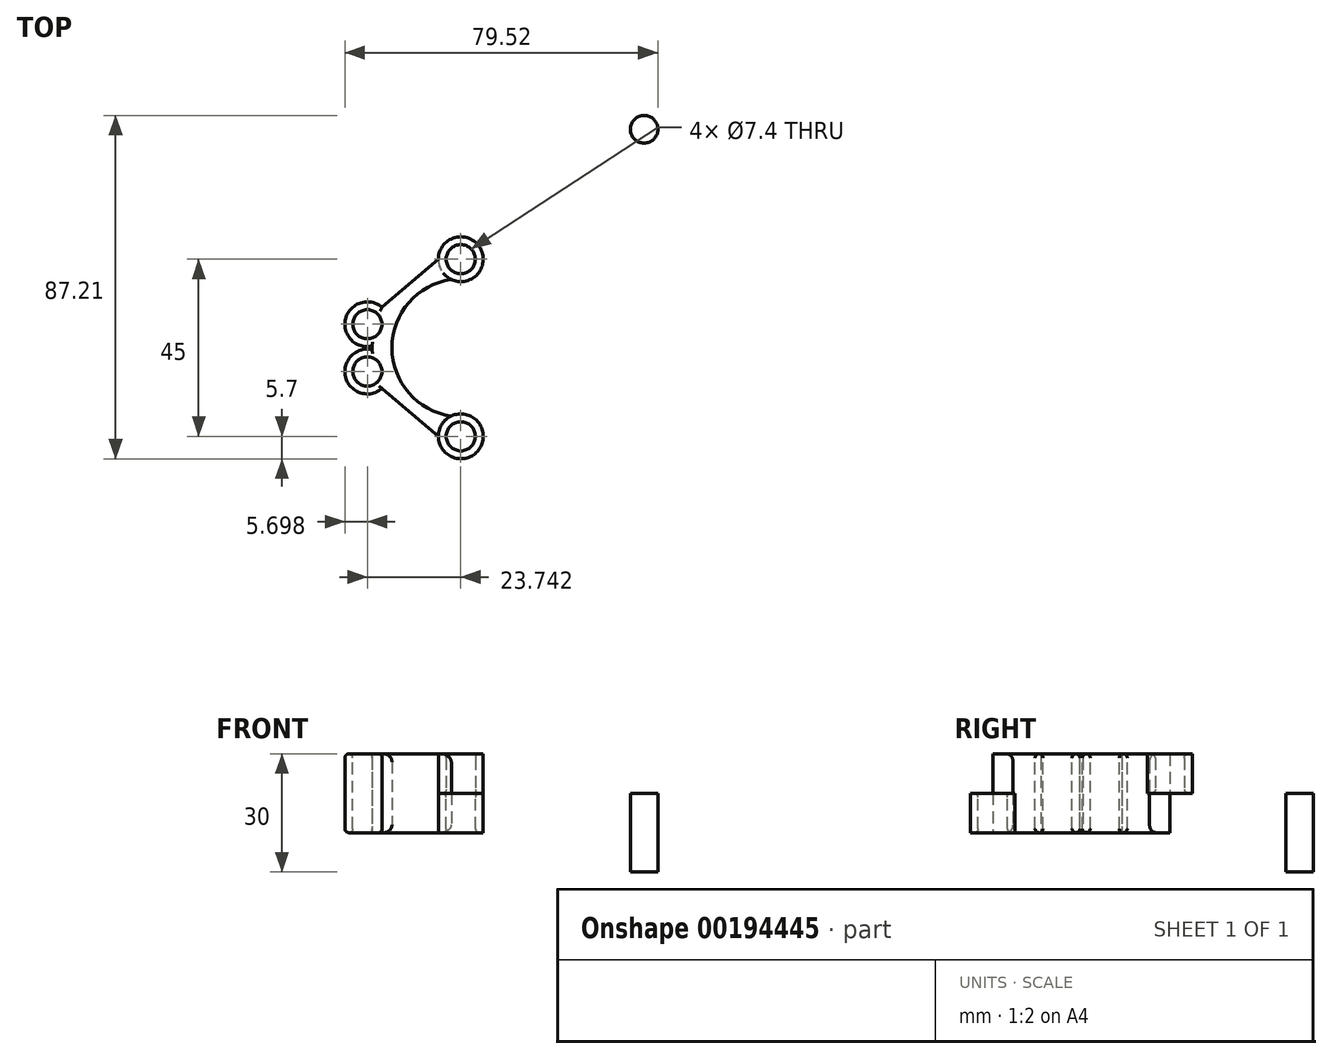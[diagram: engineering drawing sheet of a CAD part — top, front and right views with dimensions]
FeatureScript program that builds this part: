
annotation { "Feature Type Name" : "Feature", "Feature Type Description" : "" }
export const myFeature = defineFeature(function(context is Context, id is Id, definition is map)
    precondition{}
    {
        {
            var Q0;
            Q0=qCreatedBy(makeId("Top.planeOp"),FACE);
            var sketch = newSketch(context, id + "F0", { "sketchPlane" : qUnion([Q0])});
            skArc(sketch, "E0", {"start": v(-2.4, 17.33) * mm, "mid": v(-17.5, 0) * mm, "end": v(-2.4, -17.33) * mm});
            skArc(sketch, "E1", {"start": v(-20, 10.3) * mm, "mid": v(-22.5, 0) * mm, "end": v(-20, -10.3) * mm});
            skCircle(sketch, "E2", {"center": v(0, 22.5) * mm, "radius": 3.7 * mm});
            skCircle(sketch, "E3", {"center": v(0, 22.5) * mm, "radius": 5.7 * mm});
            skLineSegment(sketch, "E4", {"start": v(-5.7, 22.5) * mm, "end": v(-20, 10.3) * mm});
            skCircle(sketch, "E5", {"center": v(0, -22.5) * mm, "radius": 5.7 * mm});
            skCircle(sketch, "E6", {"center": v(0, -22.5) * mm, "radius": 3.7 * mm});
            skLineSegment(sketch, "E7", {"start": v(-5.7, -22.5) * mm, "end": v(-20, -10.3) * mm});
            skCircle(sketch, "E8", {"center": v(46.58, 55.51) * mm, "radius": 3.5 * mm});
            skCircle(sketch, "E9", {"center": v(-23.74, 5.96) * mm, "radius": 5.7 * mm});
            skCircle(sketch, "E10", {"center": v(-23.74, 5.96) * mm, "radius": 3.7 * mm});
            skCircle(sketch, "E11", {"center": v(-23.74, -6.04) * mm, "radius": 3.7 * mm});
            skCircle(sketch, "E12", {"center": v(-23.74, -6.04) * mm, "radius": 5.7 * mm});
            skSolve(sketch);
        }
        {
            var Q0;
            Q0=makeQuery(id+"F0.imprint","IMPRINT",FACE,{"disambiguationData":[TD([[makeQuery(id+"F0.imprint","IMPRINT",EDGE,{"derivedFrom":sQuery(id+"F0.wireOp",EDGE,"E0")}),-1.0]])]});
            extrude(context, id + "F1", {"entities" : qUnion([Q0]), "depth" : 20 * mm, "symmetric" : true});
        }
        {
            var Q0;
            Q0=makeQuery(id+"F0.imprint","IMPRINT",FACE,{"disambiguationData":[TD([[makeQuery(id+"F0.imprint","IMPRINT",EDGE,{"derivedFrom":sQuery(id+"F0.wireOp",EDGE,"E2")}),-1.0]])]});
            extrude(context, id + "F2", {"entities" : qUnion([Q0]), "operationType" : NewBodyOperationType.ADD, "depth" : 10 * mm});
        }
        {
            var Q0;
            Q0=makeQuery(id+"F0.imprint","IMPRINT",FACE,{"disambiguationData":[TD([[makeQuery(id+"F0.imprint","IMPRINT",EDGE,{"derivedFrom":sQuery(id+"F0.wireOp",EDGE,"E6")}),-1.0]])]});
            extrude(context, id + "F3", {"entities" : qUnion([Q0]), "operationType" : NewBodyOperationType.ADD, "oppositeDirection" : true, "depth" : 10 * mm});
        }
        {
            var Q0;
            Q0=makeQuery(id+"F0.imprint","IMPRINT",FACE,{"disambiguationData":[TD([[makeQuery(id+"F0.imprint","IMPRINT",EDGE,{"derivedFrom":sQuery(id+"F0.wireOp",EDGE,"E8")}),1.0]])]});
            extrude(context, id + "F4", {"entities" : qUnion([Q0]), "oppositeDirection" : true, "depth" : 20 * mm});
        }
        {
            var Q0;
            Q0=makeQuery(id+"F0.imprint","IMPRINT",FACE,{"disambiguationData":[TD([[makeQuery(id+"F0.imprint","IMPRINT",EDGE,{"derivedFrom":sQuery(id+"F0.wireOp",EDGE,"E11")}),-1.0]])]});
            extrude(context, id + "F5", {"entities" : qUnion([Q0]), "operationType" : NewBodyOperationType.ADD, "oppositeDirection" : true, "depth" : 10 * mm, "hasSecondDirection" : true, "secondDirectionOppositeDirection" : false, "secondDirectionDepth" : 10 * mm});
        }
        {
            var Q0;
            Q0=makeQuery(id+"F0.imprint","IMPRINT",FACE,{"disambiguationData":[TD([[makeQuery(id+"F0.imprint","IMPRINT",EDGE,{"derivedFrom":sQuery(id+"F0.wireOp",EDGE,"E9")}),1.0]])]});
            extrude(context, id + "F6", {"entities" : qUnion([Q0]), "operationType" : NewBodyOperationType.ADD, "oppositeDirection" : true, "depth" : 10 * mm, "hasSecondDirection" : true, "secondDirectionOppositeDirection" : false, "secondDirectionDepth" : 10 * mm});
        }
        {
            var Q0;
            Q0=makeQuery(id+"F1.opExtrude","CAP_EDGE",EDGE,{"disambiguationData":[OSD([sQuery(id+"F0.wireOp",EDGE,"E0")])],"isStart":false});
            var Q1;
            Q1=makeQuery(id+"F1.opExtrude","CAP_EDGE",EDGE,{"disambiguationData":[OSD([sQuery(id+"F0.wireOp",EDGE,"E0")])],"isStart":true});
            fillet(context, id + "F7", {"entities" : qUnion([Q0, Q1]), "radius" : 2 * mm, "tangentPropagation" : true, "allowEdgeOverflow" : false});
        }
        {
            var Q0;
            Q0=makeQuery(id+"F6.opExtrude","CAP_EDGE",EDGE,{"disambiguationData":[OSD([sQuery(id+"F0.wireOp",EDGE,"E9")])],"isStart":true});
            var Q1;
            Q1=makeQuery(id+"F5.opExtrude","CAP_EDGE",EDGE,{"disambiguationData":[OSD([sQuery(id+"F0.wireOp",EDGE,"E12")])],"isStart":true});
            var Q2;
            {var subQ0=sQuery(id+"F0.wireOp",EDGE,"E12");Q2=makeQuery(id+"F5.boolean.opBoolean","SPLIT",EDGE,{"disambiguationData":[topologyDisambiguationEdgeConnected([makeQuery(id+"F5.opExtrude","SWEPT_FACE",FACE,{"disambiguationData":[OSD([subQ0])]})])],"derivedFrom":makeQuery(id+"F5.opExtrude","CAP_EDGE",EDGE,{"disambiguationData":[OSD([subQ0])],"isStart":false})});}
            var Q3;
            {var subQ0=sQuery(id+"F0.wireOp",EDGE,"E9");Q3=makeQuery(id+"F6.boolean.opBoolean","SPLIT",EDGE,{"disambiguationData":[topologyDisambiguationEdgeConnected([makeQuery(id+"F6.opExtrude","SWEPT_FACE",FACE,{"disambiguationData":[OSD([subQ0])]})])],"derivedFrom":makeQuery(id+"F6.opExtrude","CAP_EDGE",EDGE,{"disambiguationData":[OSD([subQ0])],"isStart":false})});}
            var Q4;
            Q4=makeQuery(id+"F3.opExtrude","CAP_EDGE",EDGE,{"disambiguationData":[OSD([sQuery(id+"F0.wireOp",EDGE,"E6")])],"isStart":true});
            var Q5;
            Q5=makeQuery(id+"F2.opExtrude","CAP_EDGE",EDGE,{"disambiguationData":[OSD([sQuery(id+"F0.wireOp",EDGE,"E2")])],"isStart":true});
            var Q6;
            Q6=makeQuery(id+"F5.opExtrude","CAP_EDGE",EDGE,{"disambiguationData":[OSD([sQuery(id+"F0.wireOp",EDGE,"E11")])],"isStart":true});
            var Q7;
            Q7=makeQuery(id+"F6.opExtrude","CAP_EDGE",EDGE,{"disambiguationData":[OSD([sQuery(id+"F0.wireOp",EDGE,"E10")])],"isStart":true});
            var Q8;
            Q8=makeQuery(id+"F5.opExtrude","CAP_EDGE",EDGE,{"disambiguationData":[OSD([sQuery(id+"F0.wireOp",EDGE,"E11")])],"isStart":false});
            var Q9;
            Q9=makeQuery(id+"F6.opExtrude","CAP_EDGE",EDGE,{"disambiguationData":[OSD([sQuery(id+"F0.wireOp",EDGE,"E10")])],"isStart":false});
            var Q10;
            Q10=makeQuery(id+"F2.opExtrude","CAP_EDGE",EDGE,{"disambiguationData":[OSD([sQuery(id+"F0.wireOp",EDGE,"E2")])],"isStart":false});
            var Q11;
            Q11=makeQuery(id+"F3.opExtrude","CAP_EDGE",EDGE,{"disambiguationData":[OSD([sQuery(id+"F0.wireOp",EDGE,"E6")])],"isStart":false});
            fillet(context, id + "F8", {"entities" : qUnion([Q0, Q1, Q2, Q3, Q4, Q5, Q6, Q7, Q8, Q9, Q10, Q11]), "radius" : 1 * mm, "tangentPropagation" : true, "allowEdgeOverflow" : false});
        }
    });
